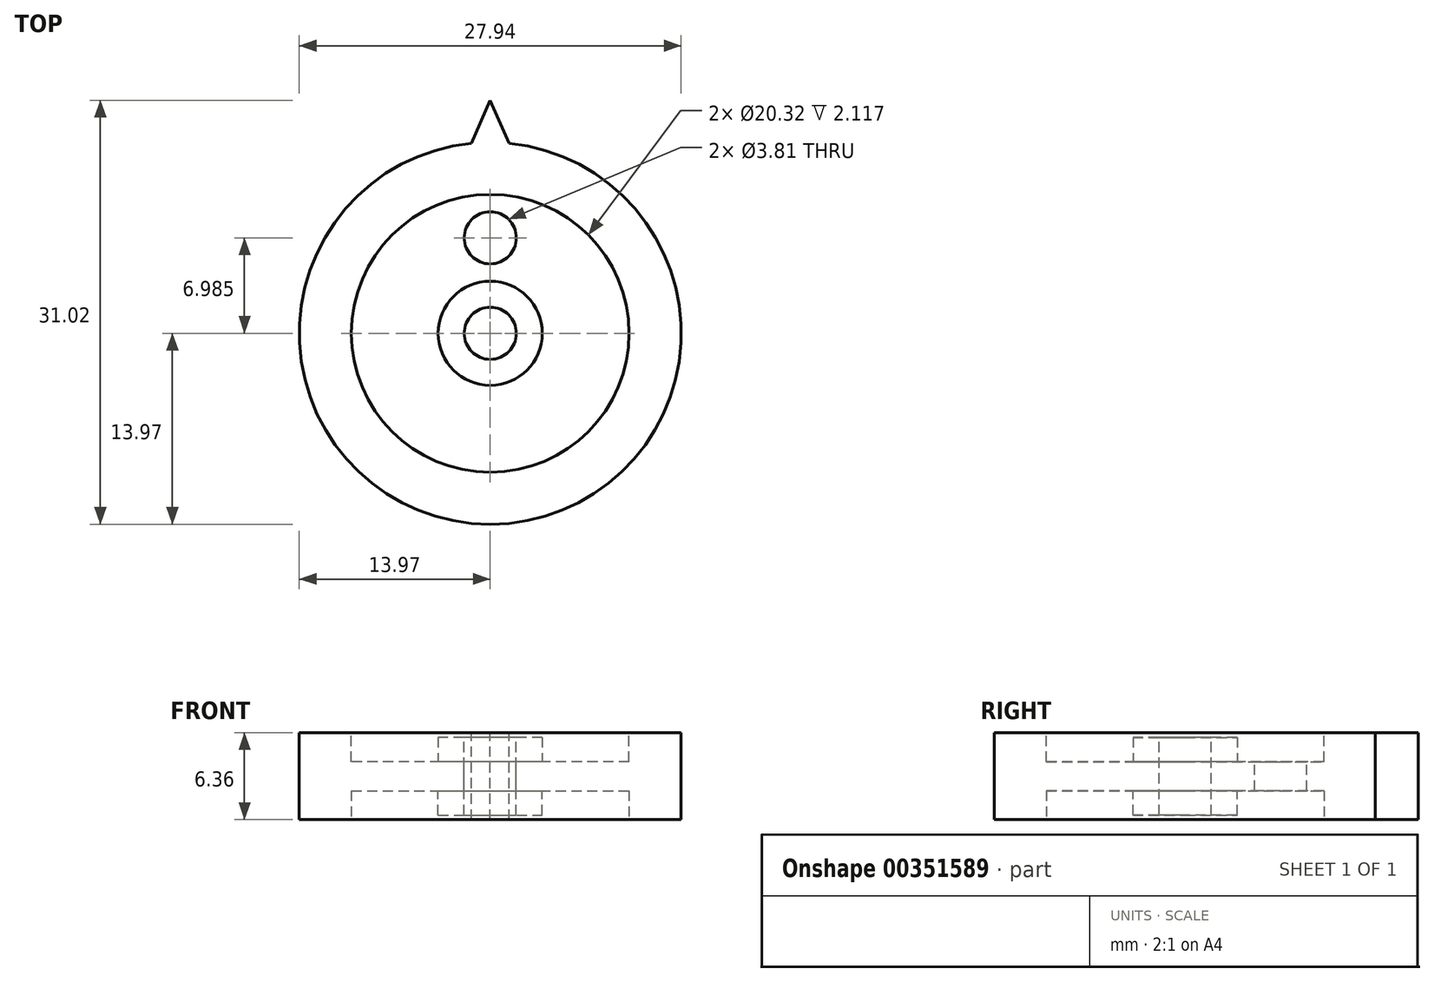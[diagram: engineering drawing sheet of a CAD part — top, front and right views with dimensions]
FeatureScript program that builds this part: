
annotation { "Feature Type Name" : "Feature", "Feature Type Description" : "" }
export const myFeature = defineFeature(function(context is Context, id is Id, definition is map)
    precondition{}
    {
        {
            var Q0;
            Q0=qCreatedBy(makeId("Top.planeOp"),FACE);
            var sketch = newSketch(context, id + "F0", { "sketchPlane" : qUnion([Q0])});
            skCircle(sketch, "E0", {"center": v(0, 0) * mm, "radius": 13.97 * mm});
            skSolve(sketch);
        }
        {
            var Q0;
            Q0 = qSketchRegion(id + "F0", true);
            extrude(context, id + "F1", {"entities" : qUnion([Q0]), "depth" : 6.35 * mm, "symmetric" : true});
        }
        {
            var Q0;
            Q0=makeQuery(id+"F1.opExtrude","CAP_FACE",FACE,{"disambiguationData":[OSD([sQuery(id+"F0.wireOp",EDGE,"E0")])],"isStart":false});
            var sketch = newSketch(context, id + "F2", { "sketchPlane" : qUnion([Q0])});
            skCircle(sketch, "E1", {"center": v(0, 0) * mm, "radius": 10.16 * mm});
            skSolve(sketch);
        }
        {
            var Q0;
            Q0 = qSketchRegion(id + "F2", true);
            extrude(context, id + "F3", {"entities" : qUnion([Q0]), "operationType" : NewBodyOperationType.REMOVE, "oppositeDirection" : true, "depth" : 2.12 * mm});
        }
        {
            var Q0;
            Q0=makeQuery(id+"F1.opExtrude","CAP_FACE",FACE,{"disambiguationData":[OSD([sQuery(id+"F0.wireOp",EDGE,"E0")])],"isStart":true});
            var sketch = newSketch(context, id + "F4", { "sketchPlane" : qUnion([Q0])});
            skCircle(sketch, "E2", {"center": v(0, 0) * mm, "radius": 10.16 * mm});
            skSolve(sketch);
        }
        {
            var Q0;
            Q0 = qSketchRegion(id + "F4", true);
            extrude(context, id + "F5", {"entities" : qUnion([Q0]), "operationType" : NewBodyOperationType.REMOVE, "oppositeDirection" : true, "depth" : 2.12 * mm});
        }
        {
            var Q0;
            Q0=makeQuery(id+"F3.boolean.opBoolean","COPY",FACE,{"derivedFrom":makeQuery(id+"F3.opExtrude","CAP_FACE",FACE,{"disambiguationData":[OSD([sQuery(id+"F2.wireOp",EDGE,"E1")])],"isStart":false})});
            var sketch = newSketch(context, id + "F6", { "sketchPlane" : qUnion([Q0])});
            skLineSegment(sketch, "E3", {"start": v(0, 0) * mm, "end": v(0, 6.99) * mm, "construction": true});
            skCircle(sketch, "E4", {"center": v(0, 6.99) * mm, "radius": 1.9 * mm});
            skSolve(sketch);
        }
        {
            var Q0;
            Q0 = qSketchRegion(id + "F6", true);
            extrude(context, id + "F7", {"entities" : qUnion([Q0]), "operationType" : NewBodyOperationType.REMOVE, "oppositeDirection" : true, "depth" : 2.54 * mm});
        }
        {
            var Q0;
            Q0=makeQuery(id+"F3.boolean.opBoolean","COPY",FACE,{"derivedFrom":makeQuery(id+"F3.opExtrude","CAP_FACE",FACE,{"disambiguationData":[OSD([sQuery(id+"F2.wireOp",EDGE,"E1")])],"isStart":false})});
            var sketch = newSketch(context, id + "F8", { "sketchPlane" : qUnion([Q0])});
            skCircle(sketch, "E5", {"center": v(0, 0) * mm, "radius": 3.81 * mm});
            skSolve(sketch);
        }
        {
            var Q0;
            Q0 = qSketchRegion(id + "F8", true);
            extrude(context, id + "F9", {"entities" : qUnion([Q0]), "operationType" : NewBodyOperationType.ADD, "depth" : 1.78 * mm});
        }
        {
            var Q0;
            Q0=makeQuery(id+"F5.boolean.opBoolean","COPY",FACE,{"derivedFrom":makeQuery(id+"F5.opExtrude","CAP_FACE",FACE,{"disambiguationData":[OSD([sQuery(id+"F4.wireOp",EDGE,"E2")])],"isStart":false})});
            var sketch = newSketch(context, id + "F10", { "sketchPlane" : qUnion([Q0])});
            skCircle(sketch, "E6", {"center": v(0, 0) * mm, "radius": 3.81 * mm});
            skSolve(sketch);
        }
        {
            var Q0;
            Q0 = qSketchRegion(id + "F10", true);
            extrude(context, id + "F11", {"entities" : qUnion([Q0]), "operationType" : NewBodyOperationType.ADD, "depth" : 1.78 * mm});
        }
        {
            var Q0;
            Q0=makeQuery(id+"F1.opExtrude","CAP_FACE",FACE,{"disambiguationData":[OSD([sQuery(id+"F0.wireOp",EDGE,"E0")])],"isStart":false});
            var sketch = newSketch(context, id + "F12", { "sketchPlane" : qUnion([Q0])});
            skLineSegment(sketch, "E7", {"start": v(-1.38, 13.9) * mm, "end": v(0, 17.05) * mm});
            skLineSegment(sketch, "E8", {"start": v(0, 17.05) * mm, "end": v(1.38, 13.9) * mm});
            skLineSegment(sketch, "E9", {"start": v(1.38, 13.9) * mm, "end": v(-1.38, 13.9) * mm});
            skSolve(sketch);
        }
        {
            var Q0;
            Q0 = qSketchRegion(id + "F12", true);
            var Q1;
            Q1=makeQuery(id+"F1.opExtrude","CAP_FACE",FACE,{"disambiguationData":[OSD([sQuery(id+"F0.wireOp",EDGE,"E0")])],"isStart":true});
            extrude(context, id + "F13", {"entities" : qUnion([Q0]), "operationType" : NewBodyOperationType.ADD, "endBound" : BoundingType.UP_TO_SURFACE, "oppositeDirection" : true, "endBoundEntityFace" : qUnion([Q1]), "depth" : 25.4 * mm});
        }
        {
            var Q0;
            Q0=makeQuery(id+"F9.opExtrude","CAP_FACE",FACE,{"disambiguationData":[OSD([sQuery(id+"F8.wireOp",EDGE,"E5")])],"isStart":false});
            var sketch = newSketch(context, id + "F14", { "sketchPlane" : qUnion([Q0])});
            skCircle(sketch, "E10", {"center": v(0, 0) * mm, "radius": 1.9 * mm});
            skSolve(sketch);
        }
        {
            var Q0;
            Q0 = qSketchRegion(id + "F14", true);
            var Q1;
            Q1=makeQuery(id+"F11.opExtrude","CAP_FACE",FACE,{"disambiguationData":[OSD([sQuery(id+"F10.wireOp",EDGE,"E6")])],"isStart":false});
            extrude(context, id + "F15", {"entities" : qUnion([Q0]), "operationType" : NewBodyOperationType.REMOVE, "endBound" : BoundingType.UP_TO_SURFACE, "oppositeDirection" : true, "endBoundEntityFace" : qUnion([Q1]), "depth" : 25.4 * mm});
        }
    });
